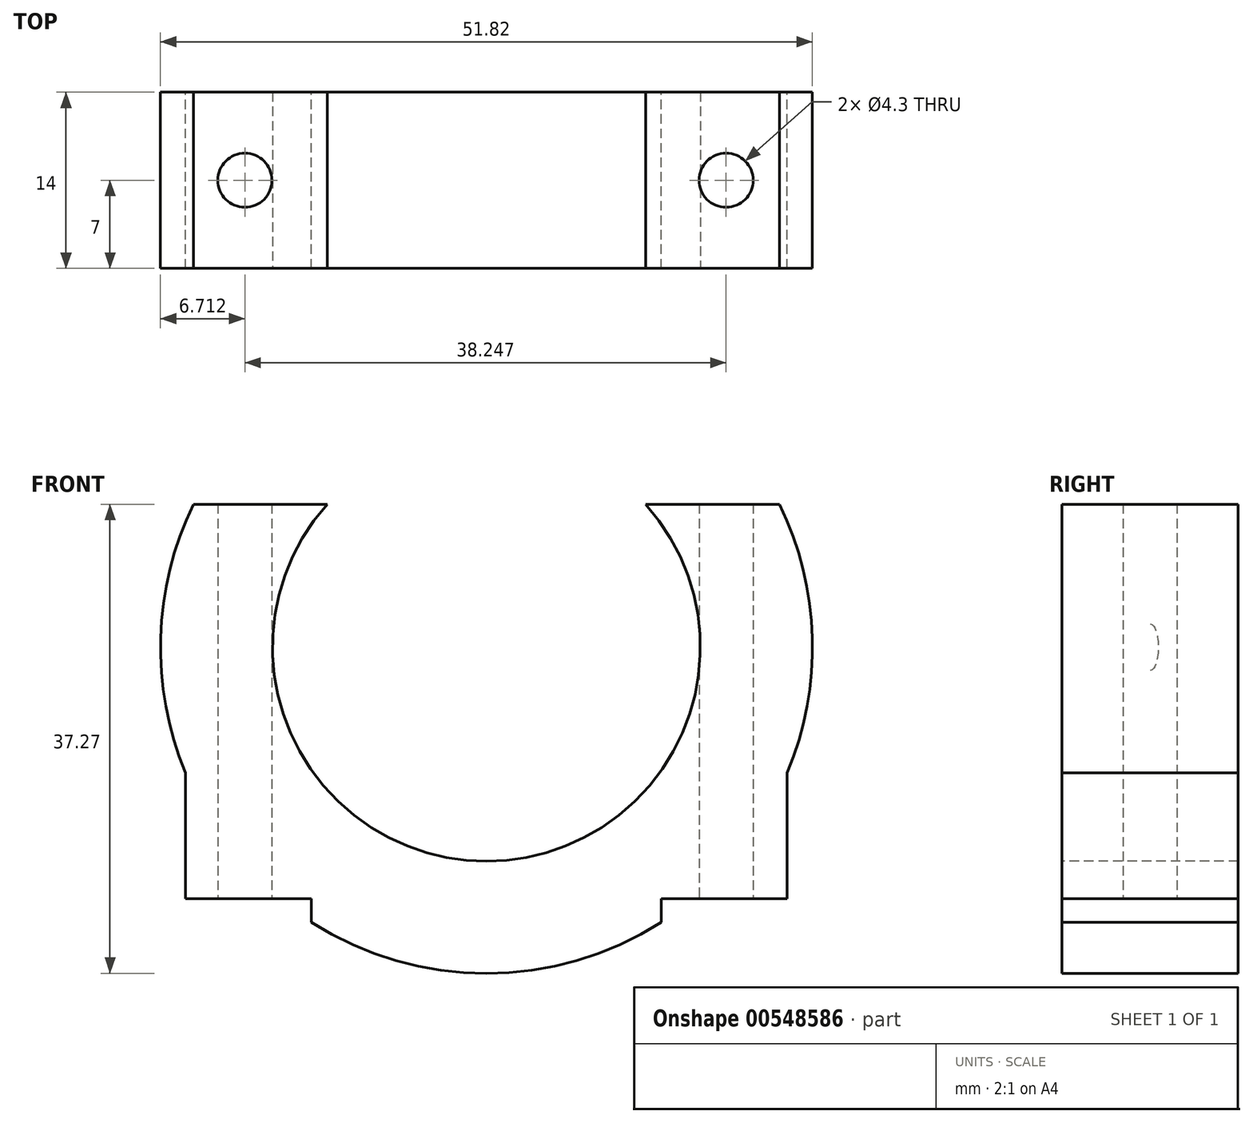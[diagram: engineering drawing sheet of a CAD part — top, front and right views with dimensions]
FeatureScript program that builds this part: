
annotation { "Feature Type Name" : "Feature", "Feature Type Description" : "" }
export const myFeature = defineFeature(function(context is Context, id is Id, definition is map)
    precondition{}
    {
        {
            var Q0;
            Q0=qCreatedBy(makeId("Front.planeOp"),FACE);
            var sketch = newSketch(context, id + "F0", { "sketchPlane" : qUnion([Q0])});
            skCircle(sketch, "E0", {"center": v(0, 0) * mm, "radius": 25.9 * mm});
            skSolve(sketch);
        }
        {
            var Q0;
            Q0 = qSketchRegion(id + "F0", true);
            extrude(context, id + "F1", {"entities" : qUnion([Q0]), "depth" : 7 * mm, "offsetDistance" : 25 * mm, "hasSecondDirection" : true, "secondDirectionOppositeDirection" : true, "secondDirectionDepth" : 7 * mm});
        }
        {
            var Q0;
            Q0=qCreatedBy(makeId("Front.planeOp"),FACE);
            var sketch = newSketch(context, id + "F2", { "sketchPlane" : qUnion([Q0])});
            skCircle(sketch, "E1", {"center": v(0, 0) * mm, "radius": 17 * mm});
            skSolve(sketch);
        }
        {
            var Q0;
            Q0 = qSketchRegion(id + "F2", true);
            extrude(context, id + "F3", {"entities" : qUnion([Q0]), "operationType" : NewBodyOperationType.REMOVE, "oppositeDirection" : true, "depth" : 7 * mm, "offsetDistance" : 25 * mm, "hasSecondDirection" : true, "secondDirectionOppositeDirection" : false, "secondDirectionDepth" : 7 * mm});
        }
        {
            var Q0;
            Q0=qCreatedBy(makeId("Top.planeOp"),FACE);
            var sketch = newSketch(context, id + "F4", { "sketchPlane" : qUnion([Q0])});
            skLineSegment(sketch, "E2.bottom", {"start": v(-62.72, 7) * mm, "end": v(62.72, 7) * mm});
            skLineSegment(sketch, "E2.top", {"start": v(-62.72, -7) * mm, "end": v(62.72, -7) * mm});
            skLineSegment(sketch, "E2.left", {"start": v(-62.72, 7) * mm, "end": v(-62.72, -7) * mm});
            skLineSegment(sketch, "E2.right", {"start": v(62.72, 7) * mm, "end": v(62.72, -7) * mm});
            skPoint(sketch, "E2.middle", {"position": v(0, 0) * mm});
            skSolve(sketch);
        }
        {
            var Q0;
            Q0=makeQuery(id+"F4.imprint","IMPRINT",FACE,{"disambiguationData":[TD([[makeQuery(id+"F4.imprint","IMPRINT",EDGE,{"derivedFrom":sQuery(id+"F4.wireOp",EDGE,"E2.bottom")}),-1.0]])]});
            var sketch = newSketch(context, id + "F5", { "sketchPlane" : qUnion([Q0])});
            skLineSegment(sketch, "E3.bottom", {"start": v(-15.9, 7) * mm, "end": v(-23.91, 7) * mm});
            skLineSegment(sketch, "E3.top", {"start": v(-15.9, -7) * mm, "end": v(-23.9, -7) * mm});
            skLineSegment(sketch, "E3.left", {"start": v(-15.9, 7) * mm, "end": v(-15.9, -7) * mm});
            skLineSegment(sketch, "E3.right", {"start": v(-23.91, 7) * mm, "end": v(-23.9, -7) * mm});
            skLineSegment(sketch, "E4.bottom", {"start": v(15.9, 7) * mm, "end": v(23.91, 7) * mm});
            skLineSegment(sketch, "E4.top", {"start": v(15.9, -7) * mm, "end": v(23.91, -7) * mm});
            skLineSegment(sketch, "E4.left", {"start": v(15.9, 7) * mm, "end": v(15.9, -7) * mm});
            skLineSegment(sketch, "E4.right", {"start": v(23.91, 7) * mm, "end": v(23.91, -7) * mm});
            skSolve(sketch);
        }
        {
            var Q0;
            Q0 = qSketchRegion(id + "F5", true);
            extrude(context, id + "F6", {"entities" : qUnion([Q0]), "operationType" : NewBodyOperationType.ADD, "oppositeDirection" : true, "depth" : 20 * mm, "offsetDistance" : 25 * mm, "hasSecondDirection" : true, "secondDirectionOppositeDirection" : true, "secondDirectionDepth" : 6 * mm});
        }
        {
            var Q0;
            Q0=makeQuery(id+"F4.imprint","IMPRINT",FACE,{"disambiguationData":[TD([[makeQuery(id+"F4.imprint","IMPRINT",EDGE,{"derivedFrom":sQuery(id+"F4.wireOp",EDGE,"E2.bottom")}),-1.0]])]});
            var sketch = newSketch(context, id + "F7", { "sketchPlane" : qUnion([Q0])});
            skCircle(sketch, "E5", {"center": v(-19.2, 0) * mm, "radius": 2.15 * mm});
            skCircle(sketch, "E6", {"center": v(19.05, 0) * mm, "radius": 2.15 * mm});
            skSolve(sketch);
        }
        {
            var Q0;
            Q0 = qSketchRegion(id + "F7", true);
            extrude(context, id + "F8", {"entities" : qUnion([Q0]), "operationType" : NewBodyOperationType.REMOVE, "depth" : 30 * mm, "offsetDistance" : 25 * mm, "hasSecondDirection" : true, "secondDirectionOppositeDirection" : true, "secondDirectionDepth" : 30 * mm});
        }
        {
            var Q0;
            Q0=makeQuery(id+"F6.opExtrude","CAP_FACE",FACE,{"disambiguationData":[OSD([sQuery(id+"F5.wireOp",EDGE,"E3.bottom"),sQuery(id+"F5.wireOp",EDGE,"E3.top"),sQuery(id+"F5.wireOp",EDGE,"E3.left"),sQuery(id+"F5.wireOp",EDGE,"E3.right")])],"isStart":false});
            var sketch = newSketch(context, id + "F9", { "sketchPlane" : qUnion([Q0])});
            skLineSegment(sketch, "E7.bottom", {"start": v(-23.91, -7) * mm, "end": v(-13.9, -7) * mm});
            skLineSegment(sketch, "E7.top", {"start": v(-23.91, 7) * mm, "end": v(-13.91, 7) * mm});
            skLineSegment(sketch, "E7.left", {"start": v(-23.91, -7) * mm, "end": v(-23.91, 7) * mm});
            skLineSegment(sketch, "E7.right", {"start": v(-13.9, -7) * mm, "end": v(-13.91, 7) * mm});
            skLineSegment(sketch, "E8.bottom", {"start": v(23.91, -7) * mm, "end": v(13.91, -7) * mm});
            skLineSegment(sketch, "E8.top", {"start": v(23.91, 7) * mm, "end": v(13.9, 7) * mm});
            skLineSegment(sketch, "E8.left", {"start": v(23.91, -7) * mm, "end": v(23.91, 7) * mm});
            skLineSegment(sketch, "E8.right", {"start": v(13.91, -7) * mm, "end": v(13.9, 7) * mm});
            skSolve(sketch);
        }
        {
            var Q0;
            Q0 = qSketchRegion(id + "F9", true);
            extrude(context, id + "F10", {"entities" : qUnion([Q0]), "operationType" : NewBodyOperationType.REMOVE, "depth" : 10 * mm, "offsetDistance" : 25 * mm});
        }
        {
            var Q0;
            Q0=makeQuery(id+"F6.boolean.opBoolean","MERGE",FACE,{"derivedFrom":[makeQuery(id+"F1.opExtrude","CAP_FACE",FACE,{"disambiguationData":[OSD([sQuery(id+"F0.wireOp",EDGE,"E0")])],"isStart":false}),makeQuery(id+"F6.opExtrude","SWEPT_FACE",FACE,{"disambiguationData":[OSD([sQuery(id+"F5.wireOp",EDGE,"E3.top")])]}),makeQuery(id+"F6.opExtrude","SWEPT_FACE",FACE,{"disambiguationData":[OSD([sQuery(id+"F5.wireOp",EDGE,"E4.top")])]})]});
            var sketch = newSketch(context, id + "F11", { "sketchPlane" : qUnion([Q0])});
            skLineSegment(sketch, "E9.bottom", {"start": v(36.26, 0) * mm, "end": v(51.82, 0) * mm});
            skLineSegment(sketch, "E9.top", {"start": v(36.26, 11.36) * mm, "end": v(51.82, 11.36) * mm});
            skLineSegment(sketch, "E9.left", {"start": v(36.26, 0) * mm, "end": v(36.26, 11.36) * mm});
            skLineSegment(sketch, "E9.right", {"start": v(51.82, 0) * mm, "end": v(51.82, 11.36) * mm});
            skSolve(sketch);
        }
        {
            var Q0;
            Q0=makeQuery(id+"F6.boolean.opBoolean","MERGE",FACE,{"derivedFrom":[makeQuery(id+"F1.opExtrude","CAP_FACE",FACE,{"disambiguationData":[OSD([sQuery(id+"F0.wireOp",EDGE,"E0")])],"isStart":true}),makeQuery(id+"F6.opExtrude","SWEPT_FACE",FACE,{"disambiguationData":[OSD([sQuery(id+"F5.wireOp",EDGE,"E3.bottom")])]}),makeQuery(id+"F6.opExtrude","SWEPT_FACE",FACE,{"disambiguationData":[OSD([sQuery(id+"F5.wireOp",EDGE,"E4.bottom")])]})]});
            var sketch = newSketch(context, id + "F12", { "sketchPlane" : qUnion([Q0])});
            skLineSegment(sketch, "E10", {"start": v(-48.16, 0) * mm, "end": v(-48.16, 11.36) * mm});
            skSolve(sketch);
        }
        {
            var Q0;
            Q0=sQuery(id+"F11.wireOp",VERTEX,"E9.right.end");
            var Q1;
            Q1=sQuery(id+"F12.wireOp",VERTEX,"E10.end");
            var Q2;
            Q2=sQuery(id+"F11.wireOp",VERTEX,"E9.left.end");
            cPlane(context, id + "F13", {"entities" : qUnion([Q0, Q1, Q2]), "cplaneType" : CPlaneType.THREE_POINT, "offset" : 25 * mm, "width" : 150 * mm, "height" : 150 * mm});
        }
        {
            var Q0;
            Q0=qCreatedBy(id+"F13.planeOp",FACE);
            var sketch = newSketch(context, id + "F14", { "sketchPlane" : qUnion([Q0])});
            skLineSegment(sketch, "E11.bottom", {"start": v(70.32, 38.8) * mm, "end": v(-52.4, 38.8) * mm});
            skLineSegment(sketch, "E11.top", {"start": v(70.32, -46.16) * mm, "end": v(-52.4, -46.16) * mm});
            skLineSegment(sketch, "E11.left", {"start": v(70.32, 38.8) * mm, "end": v(70.32, -46.16) * mm});
            skLineSegment(sketch, "E11.right", {"start": v(-52.4, 38.8) * mm, "end": v(-52.4, -46.16) * mm});
            skSolve(sketch);
        }
        {
            var Q0;
            Q0 = qSketchRegion(id + "F14", true);
            extrude(context, id + "F15", {"entities" : qUnion([Q0]), "operationType" : NewBodyOperationType.REMOVE, "oppositeDirection" : true, "depth" : 18 * mm, "offsetDistance" : 25 * mm});
        }
    });
